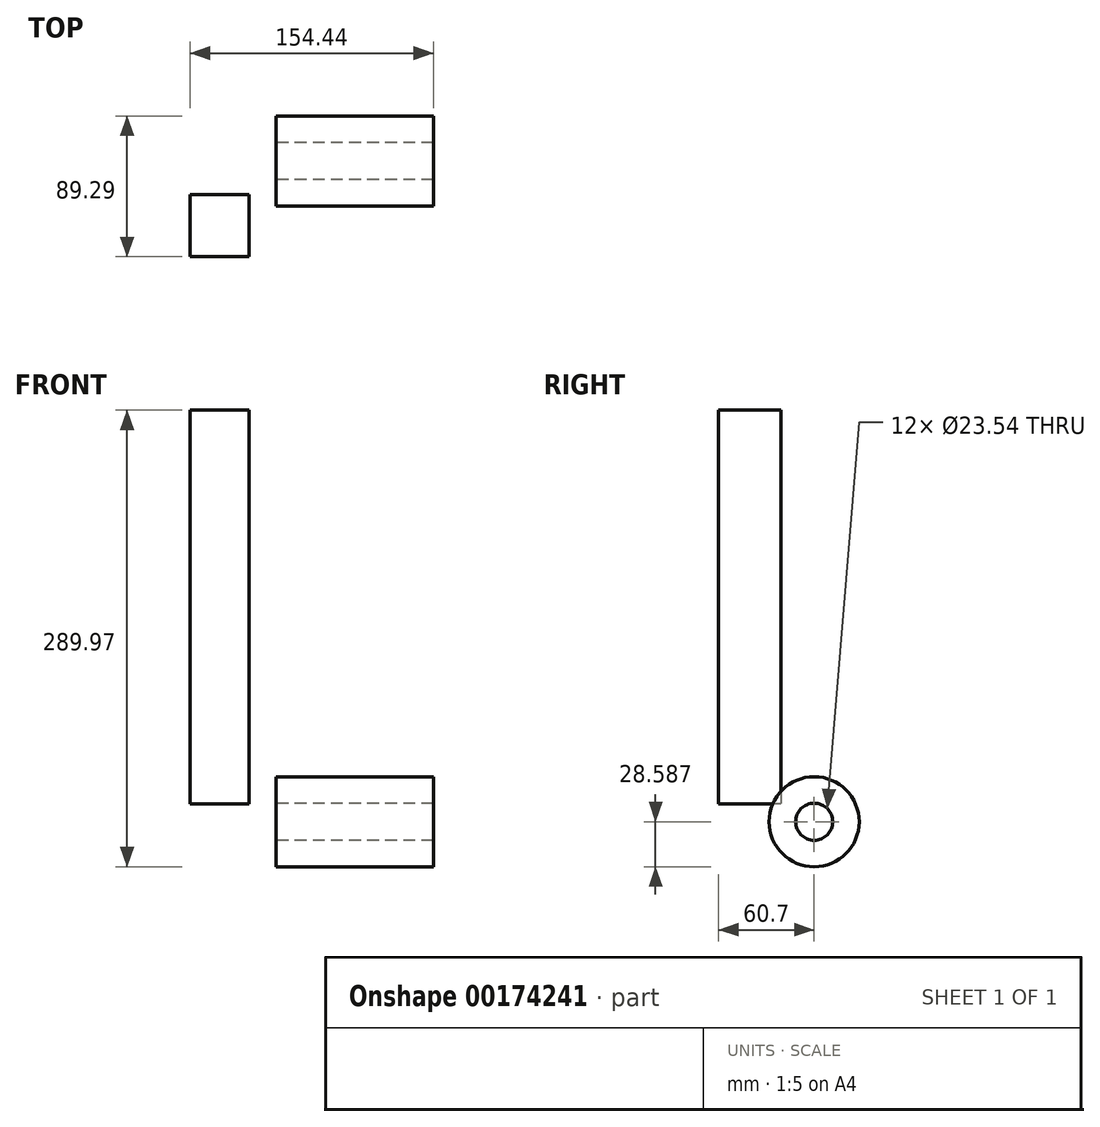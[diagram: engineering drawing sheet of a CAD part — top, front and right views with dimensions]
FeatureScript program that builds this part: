
annotation { "Feature Type Name" : "Feature", "Feature Type Description" : "" }
export const myFeature = defineFeature(function(context is Context, id is Id, definition is map)
    precondition{}
    {
        {
            var Q0;
            Q0=qCreatedBy(makeId("Top.planeOp"),FACE);
            var sketch = newSketch(context, id + "F0", { "sketchPlane" : qUnion([Q0])});
            skLineSegment(sketch, "E0.bottom", {"start": v(-54.44, -7.47) * mm, "end": v(-17.05, -7.47) * mm});
            skLineSegment(sketch, "E0.top", {"start": v(-54.44, -46.98) * mm, "end": v(-17.05, -46.98) * mm});
            skLineSegment(sketch, "E0.left", {"start": v(-54.44, -7.47) * mm, "end": v(-54.44, -46.98) * mm});
            skLineSegment(sketch, "E0.right", {"start": v(-17.05, -7.47) * mm, "end": v(-17.05, -46.98) * mm});
            skSolve(sketch);
        }
        {
            var Q0;
            Q0=qCreatedBy(makeId("Right.planeOp"),FACE);
            var sketch = newSketch(context, id + "F1", { "sketchPlane" : qUnion([Q0])});
            skCircle(sketch, "E1", {"center": v(13.72, -11.38) * mm, "radius": 28.59 * mm});
            skCircle(sketch, "E2", {"center": v(13.72, -11.38) * mm, "radius": 11.77 * mm});
            skSolve(sketch);
        }
        {
            var Q0;
            Q0 = qSketchRegion(id + "F1", true);
            extrude(context, id + "F2", {"entities" : qUnion([Q0]), "depth" : 100 * mm});
        }
        {
            var Q0;
            Q0=makeQuery(id+"F0.imprint","IMPRINT",FACE,{"disambiguationData":[TD([[makeQuery(id+"F0.imprint","IMPRINT",EDGE,{"derivedFrom":sQuery(id+"F0.wireOp",EDGE,"E0.bottom")}),-1.0]])]});
            extrude(context, id + "F3", {"entities" : qUnion([Q0]), "depth" : 250 * mm});
        }
    });
